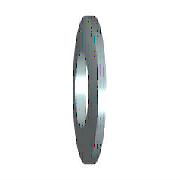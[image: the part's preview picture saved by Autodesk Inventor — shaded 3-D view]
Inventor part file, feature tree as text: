
AUTODESK INVENTOR PART (.ipt)
format: ipt  version: 2017 (Build 210142000, 142)  size: 117,760 bytes
history: native  units: mm (DEFAULTED — no unit token found)
features: other x2, plane x1
ambient origin geometry x7: Origin, YZ Plane, XY Plane, X Axis, Y Axis, Z Axis, Center Point
bodies: Solid1 (feature_tree)
feature tree (3):
  other  "IDS_BODY"
  other  "Work Axis1"
  plane  "Work Plane1"
